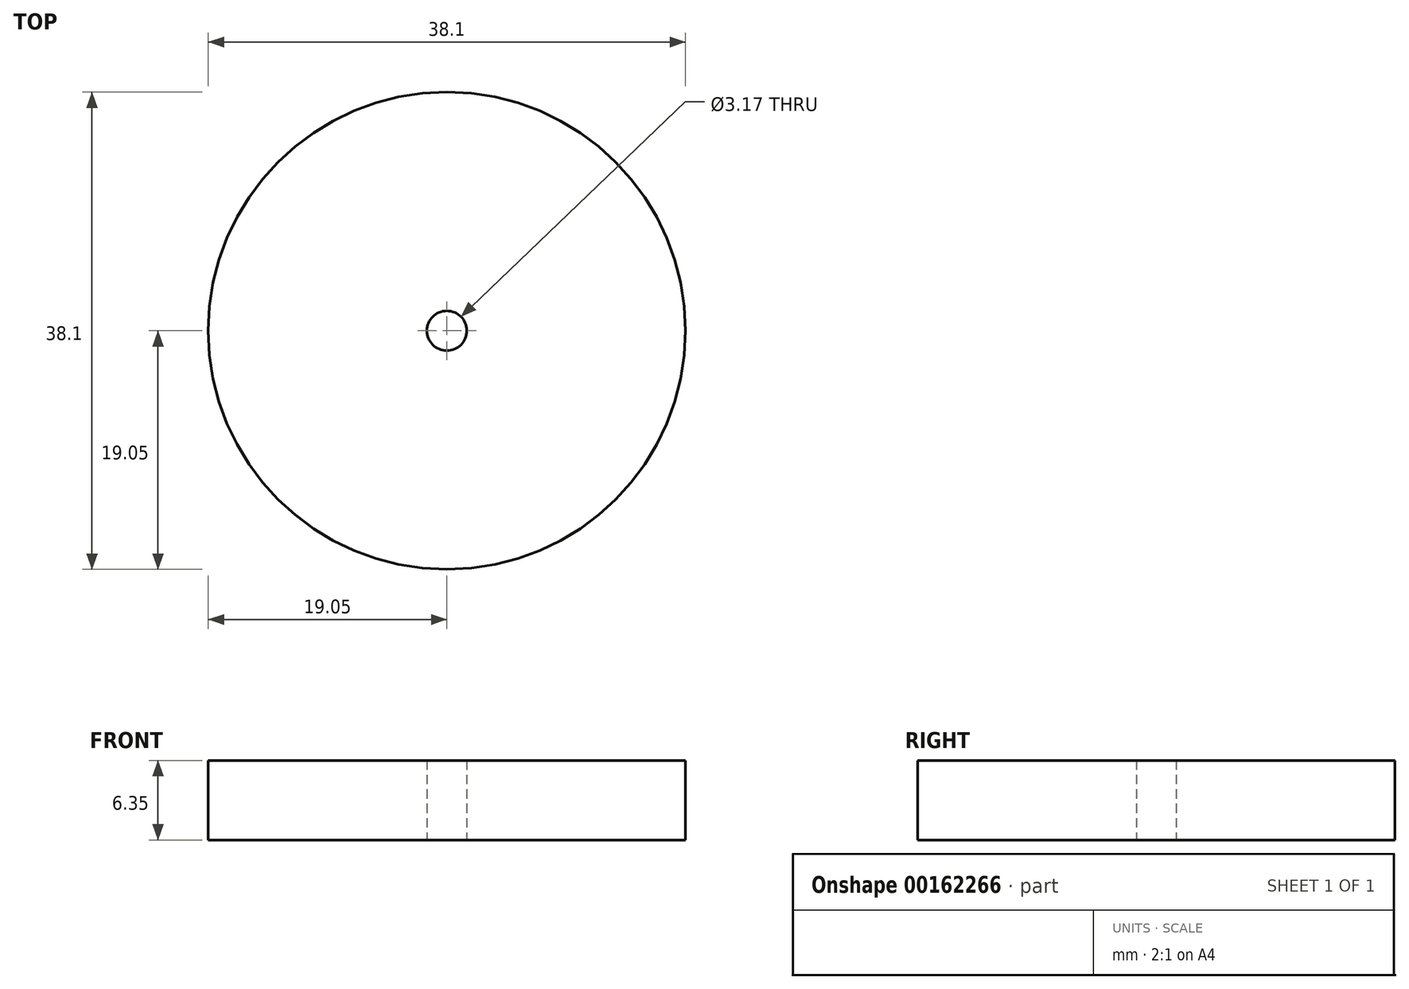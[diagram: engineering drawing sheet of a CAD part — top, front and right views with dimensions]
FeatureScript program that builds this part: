
annotation { "Feature Type Name" : "Feature", "Feature Type Description" : "" }
export const myFeature = defineFeature(function(context is Context, id is Id, definition is map)
    precondition{}
    {
        {
            var Q0;
            Q0=qCreatedBy(makeId("Top.planeOp"),FACE);
            var sketch = newSketch(context, id + "F0", { "sketchPlane" : qUnion([Q0])});
            skCircle(sketch, "E0", {"center": v(0, 0) * mm, "radius": 19.05 * mm});
            skCircle(sketch, "E1", {"center": v(0, 0) * mm, "radius": 1.59 * mm});
            skSolve(sketch);
        }
        {
            var Q0;
            Q0=makeQuery(id+"F0.imprint","IMPRINT",FACE,{"disambiguationData":[TD([[makeQuery(id+"F0.imprint","IMPRINT",EDGE,{"derivedFrom":sQuery(id+"F0.wireOp",EDGE,"E0")}),1.0]])]});
            extrude(context, id + "F1", {"entities" : qUnion([Q0]), "depth" : 6.35 * mm});
        }
    });
